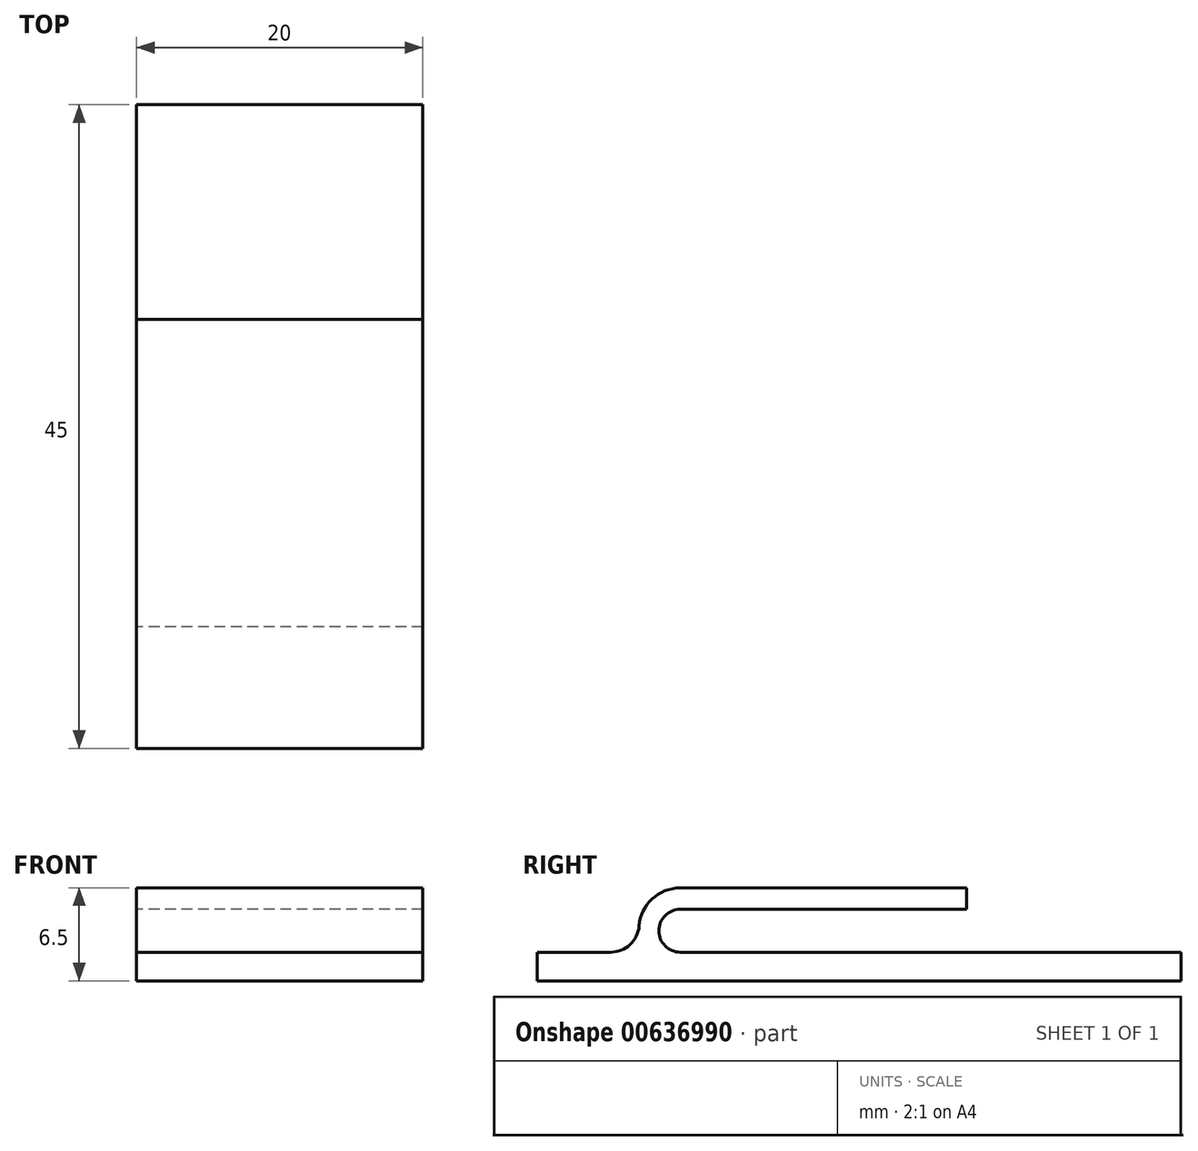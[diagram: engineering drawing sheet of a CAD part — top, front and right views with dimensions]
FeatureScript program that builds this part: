
annotation { "Feature Type Name" : "Feature", "Feature Type Description" : "" }
export const myFeature = defineFeature(function(context is Context, id is Id, definition is map)
    precondition{}
    {
        {
            var Q0;
            Q0=qCreatedBy(makeId("Right.planeOp"),FACE);
            var sketch = newSketch(context, id + "F0", { "sketchPlane" : qUnion([Q0])});
            skLineSegment(sketch, "E0", {"start": v(0, 0) * mm, "end": v(45, 0) * mm});
            skLineSegment(sketch, "E1", {"start": v(45, 0) * mm, "end": v(45, 2) * mm});
            skLineSegment(sketch, "E2", {"start": v(45, 2) * mm, "end": v(10, 2) * mm});
            skArc(sketch, "E3", {"start": v(10, 2) * mm, "mid": v(8.5, 3.5) * mm, "end": v(10, 5) * mm});
            skLineSegment(sketch, "E4", {"start": v(10, 5) * mm, "end": v(30, 5) * mm});
            skLineSegment(sketch, "E5", {"start": v(30, 5) * mm, "end": v(30, 6.5) * mm});
            skLineSegment(sketch, "E6", {"start": v(30, 6.5) * mm, "end": v(10, 6.5) * mm});
            skLineSegment(sketch, "E7", {"start": v(0, 0) * mm, "end": v(0, 2) * mm});
            skLineSegment(sketch, "E8", {"start": v(0, 2) * mm, "end": v(5.13, 2) * mm});
            skArc(sketch, "E9", {"start": v(10, 6.5) * mm, "mid": v(8.04, 5.73) * mm, "end": v(7.12, 3.84) * mm});
            skPoint(sketch, "E10.visualSharp", {"position": v(7.6, 2) * mm});
            skArc(sketch, "E10.filletArc", {"start": v(5.13, 2) * mm, "mid": v(6.49, 2.53) * mm, "end": v(7.12, 3.84) * mm});
            skSolve(sketch);
        }
        {
            var Q0;
            Q0 = qSketchRegion(id + "F0", true);
            extrude(context, id + "F1", {"entities" : qUnion([Q0]), "depth" : 20 * mm, "offsetDistance" : 25 * mm});
        }
    });
